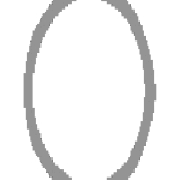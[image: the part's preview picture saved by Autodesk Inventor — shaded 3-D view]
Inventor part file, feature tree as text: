
AUTODESK INVENTOR PART (.ipt)
format: ipt  version: 2021 (Build 250183000, 183)  size: 112,128 bytes
history: native  units: in
note: dims shown in document units (in); Inventor stores cm internally (conversion verified against a paired STEP export)
features: other x4, sketch x3, plane x1
ambient origin geometry x8: Origin, YZ Plane, XZ Plane, XY Plane, X Axis, Y Axis, Z Axis, Center Point
bodies: Solid1 (feature_tree), Body (feature_tree)
feature tree (8):
  other  "Driven Length"
  other  "Frame Generator"
  other  "Start Plane"
  other  "End Plane"
  sketch  "Sketch"  dims[d2=14.4375in d4=-0.0in d5=14.4375in d6=0.12in d7=0.0in d8=90.0deg d9=14.4375in]
  sketch  "Sketch2"  dims[d0=1.0in]
  plane  "Work Plane3"
  sketch  "Sketch3"  dims[d1=0.065in]
